# Revit family: 4 X B2HE 199 with 200-120 LLH
name_source: partatom
category: Mechanical Equipment
units: mm (PartAtom-declared; Revit-internal decimal feet)

## family parameters
Always vertical = Yes
Classification = None
Cut with Voids When Loaded = No
OmniClass Number = 23.75.10.11.14.14
OmniClass Title = Condensing Boilers
Part Type = Normal
Room Calculation Point = No
Round Connector Dimension = Use Diameter
Shared = No
Work Plane-Based = No

## types (1)
- Standard
    Connector_11_Diameter = 0' - 3"
    Connector_12_Diameter = 0' - 3"
    Connector_13_Diameter = 0' - 3"
    Connector_14_Diameter = 0' - 3"
    Connector_15_Diameter = 0' - 5"
    Connector_16_Diameter = 0' - 5"
    Connector_17_Diameter = 0' - 5"
    Connector_18_Diameter = 0' - 5"
    Connector_19_Diameter = 0' - 3"
    Connector_1_Diameter = 0' - 3"
    Connector_20_Diameter = 0' - 3"
    Connector_21_Diameter = 0' - 3"
    Connector_22_Diameter = 0' - 3"
    Connector_23_Diameter = 0' - 3"
    Connector_24_Diameter = 0' - 3"
    Connector_25_Diameter = 0' - 3"
    Connector_26_Diameter = 0' - 3"
    Connector_2_Diameter = 0' - 3"
    Connector_3_Diameter = 0' - 0 3/4"
    Connector_4_Diameter = 0' - 0 3/4"
    Connector_5_Diameter = 0' - 0 3/4"
    Connector_6_Diameter = 0' - 0 3/4"
    Default Elevation = 0' - 0"
    Description = 4 Boiler Distribution Manifold
    Manufacturer = Viessmann
    Model = 4 X Vitodens 200 B2HE 199
    URL = www.viessmann.com

## geometry (parser evidence)
native form markers: Sweep x2
no freeform markers — native parametric forms only
